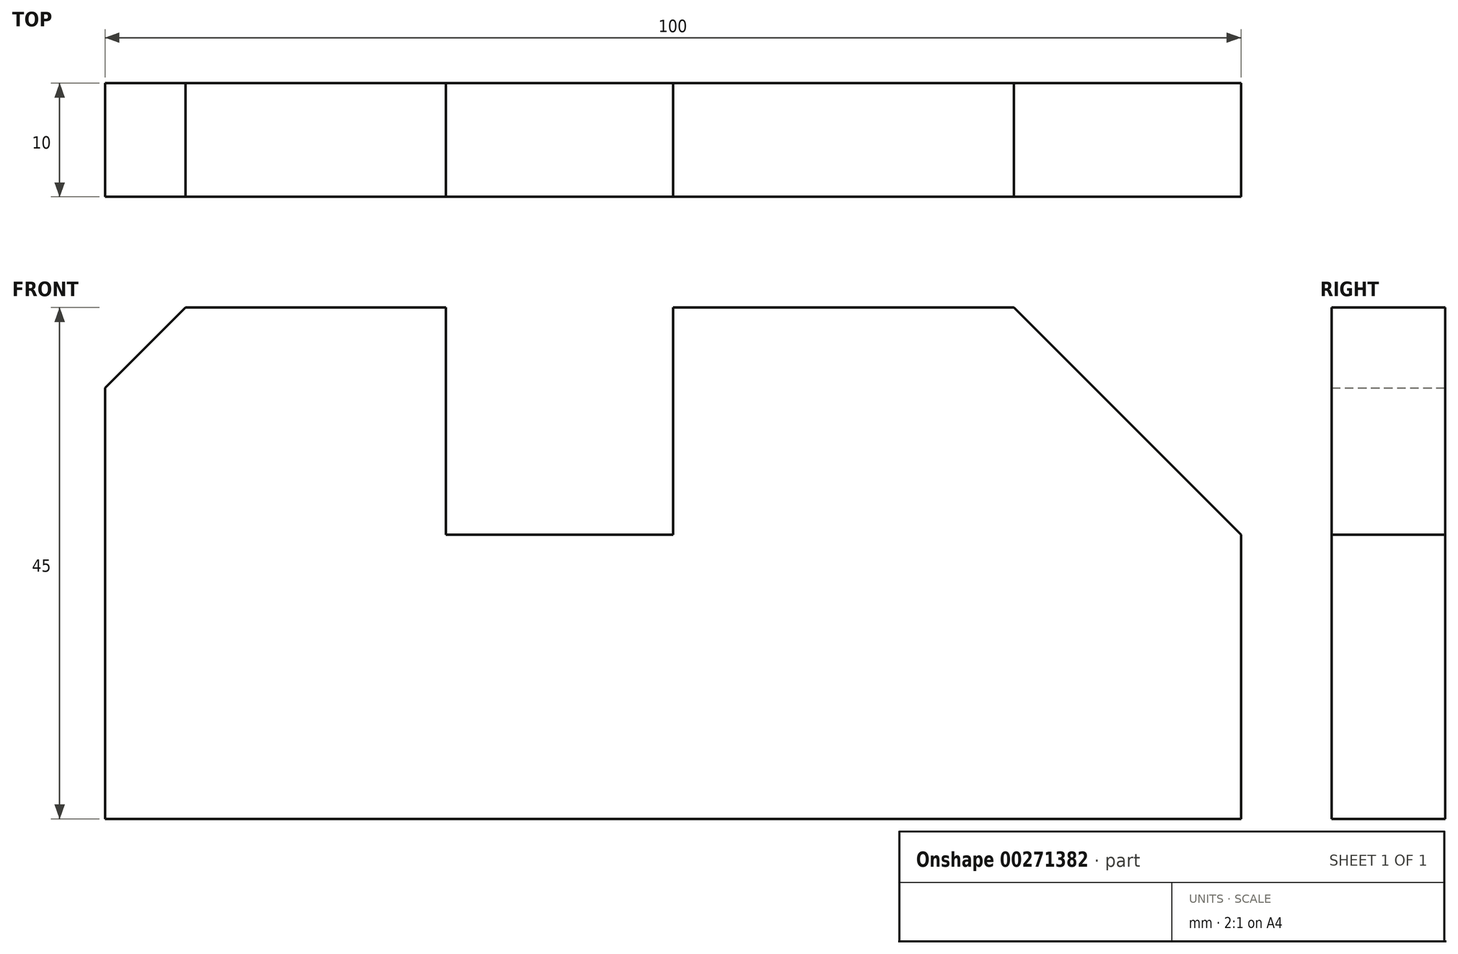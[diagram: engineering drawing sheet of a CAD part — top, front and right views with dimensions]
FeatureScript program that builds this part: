
annotation { "Feature Type Name" : "Feature", "Feature Type Description" : "" }
export const myFeature = defineFeature(function(context is Context, id is Id, definition is map)
    precondition{}
    {
        {
            var Q0;
            Q0=qCreatedBy(makeId("Front.planeOp"),FACE);
            var sketch = newSketch(context, id + "F0", { "sketchPlane" : qUnion([Q0])});
            skLineSegment(sketch, "E0", {"start": v(7.07, 45) * mm, "end": v(30, 45) * mm});
            skLineSegment(sketch, "E1", {"start": v(30, 45) * mm, "end": v(30, 25) * mm});
            skLineSegment(sketch, "E2", {"start": v(30, 25) * mm, "end": v(50, 25) * mm});
            skLineSegment(sketch, "E3", {"start": v(50, 25) * mm, "end": v(50, 45) * mm});
            skLineSegment(sketch, "E4", {"start": v(50, 45) * mm, "end": v(80, 45) * mm});
            skLineSegment(sketch, "E5", {"start": v(80, 45) * mm, "end": v(100, 25) * mm});
            skLineSegment(sketch, "E6", {"start": v(100, 25) * mm, "end": v(100, 0) * mm});
            skLineSegment(sketch, "E7", {"start": v(100, 0) * mm, "end": v(0, 0) * mm});
            skLineSegment(sketch, "E8", {"start": v(7.07, 45) * mm, "end": v(0, 37.93) * mm});
            skLineSegment(sketch, "E9", {"start": v(0, 37.93) * mm, "end": v(0, 0) * mm});
            skSolve(sketch);
        }
        {
            var Q0;
            Q0 = qSketchRegion(id + "F0", true);
            extrude(context, id + "F1", {"entities" : qUnion([Q0]), "depth" : 10 * mm});
        }
    });
